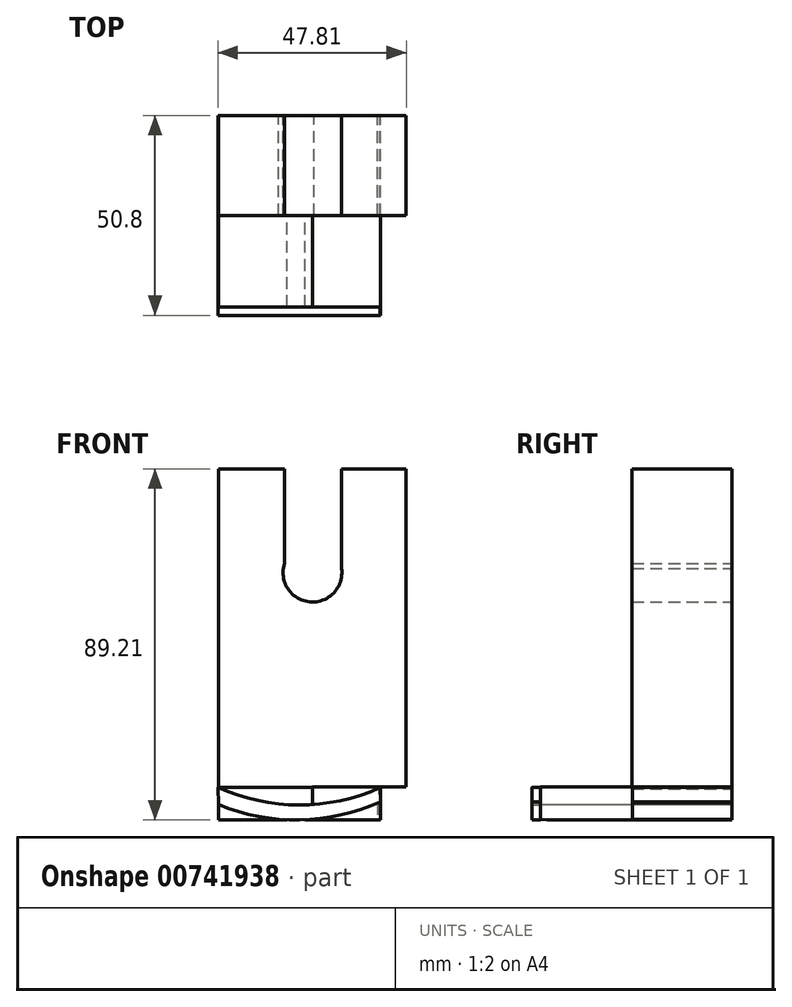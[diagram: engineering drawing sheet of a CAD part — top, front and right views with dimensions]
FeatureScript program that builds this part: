
annotation { "Feature Type Name" : "Feature", "Feature Type Description" : "" }
export const myFeature = defineFeature(function(context is Context, id is Id, definition is map)
    precondition{}
    {
        {
            var Q0;
            Q0=qCreatedBy(makeId("Front.planeOp"),FACE);
            var sketch = newSketch(context, id + "F0", { "sketchPlane" : qUnion([Q0])});
            skLineSegment(sketch, "E0.bottom", {"start": v(23.82, 44.5) * mm, "end": v(-23.82, 44.5) * mm});
            skLineSegment(sketch, "E0.top", {"start": v(16.53, -44.5) * mm, "end": v(-23.82, -44.5) * mm});
            skLineSegment(sketch, "E0.left", {"start": v(23.82, 44.5) * mm, "end": v(23.82, -36.31) * mm});
            skLineSegment(sketch, "E0.right", {"start": v(-23.82, 44.5) * mm, "end": v(-23.82, -44.5) * mm});
            skPoint(sketch, "E0.middle", {"position": v(0, 0) * mm});
            skLineSegment(sketch, "E1.bottom", {"start": v(-7.1, 44.5) * mm, "end": v(7.4, 44.5) * mm});
            skLineSegment(sketch, "E1.top", {"start": v(0, 18.15) * mm, "end": v(0.15, 18.15) * mm});
            skLineSegment(sketch, "E1.left", {"start": v(-7.1, 44.5) * mm, "end": v(-7.1, 18.15) * mm});
            skLineSegment(sketch, "E1.right", {"start": v(7.4, 44.5) * mm, "end": v(7.4, 18.15) * mm});
            skArc(sketch, "E2", {"start": v(-7.1, 20.49) * mm, "mid": v(-0.68, 10.7) * mm, "end": v(7.4, 19.17) * mm});
            skPoint(sketch, "E2.centerSnap0", {"position": v(0.15, 18.15) * mm});
            skLineSegment(sketch, "E3", {"start": v(23.82, -36.31) * mm, "end": v(16.53, -36.31) * mm});
            skLineSegment(sketch, "E4", {"start": v(16.53, -36.31) * mm, "end": v(16.53, -44.5) * mm});
            skPoint(sketch, "E5.orphan", {"position": v(23.82, -44.5) * mm});
            skSolve(sketch);
        }
        {
            var Q0;
            Q0=makeQuery(id+"F0.imprint","IMPRINT",FACE,{"disambiguationData":[TD([[makeQuery(id+"F0.imprint","IMPRINT",EDGE,{"derivedFrom":sQuery(id+"F0.wireOp",EDGE,"E0.top")}),-1.0]])]});
            extrude(context, id + "F1", {"entities" : qUnion([Q0]), "depth" : 25.4 * mm, "offsetDistance" : 25.4 * mm});
        }
        {
            var Q0;
            Q0=qCreatedBy(makeId("Right.planeOp"),FACE);
            var sketch = newSketch(context, id + "F2", { "sketchPlane" : qUnion([Q0])});
            skLineSegment(sketch, "E6", {"start": v(-25.4, -36.35) * mm, "end": v(-48.64, -36.35) * mm});
            skLineSegment(sketch, "E7", {"start": v(-48.64, -36.35) * mm, "end": v(-48.64, -44.71) * mm});
            skLineSegment(sketch, "E8", {"start": v(-48.64, -44.71) * mm, "end": v(-25.33, -44.58) * mm});
            skLineSegment(sketch, "E9", {"start": v(-25.33, -44.58) * mm, "end": v(-25.4, -36.35) * mm});
            skSolve(sketch);
        }
        {
            var Q0;
            Q0=makeQuery(id+"F2.imprint","IMPRINT",FACE,{"disambiguationData":[TD([[makeQuery(id+"F2.imprint","IMPRINT",EDGE,{"derivedFrom":sQuery(id+"F2.wireOp",EDGE,"E6")}),1.0]])]});
            extrude(context, id + "F3", {"entities" : qUnion([Q0]), "operationType" : NewBodyOperationType.ADD, "depth" : 17.27 * mm, "offsetDistance" : 25.4 * mm});
        }
        {
            var Q0;
            Q0=qCreatedBy(makeId("Right.planeOp"),FACE);
            var sketch = newSketch(context, id + "F4", { "sketchPlane" : qUnion([Q0])});
            skLineSegment(sketch, "E10.bottom", {"start": v(-25.35, -36.37) * mm, "end": v(-48.66, -36.37) * mm});
            skLineSegment(sketch, "E10.top", {"start": v(-25.35, -44.65) * mm, "end": v(-48.66, -44.65) * mm});
            skLineSegment(sketch, "E10.left", {"start": v(-25.35, -36.37) * mm, "end": v(-25.35, -44.65) * mm});
            skLineSegment(sketch, "E10.right", {"start": v(-48.66, -36.37) * mm, "end": v(-48.66, -44.65) * mm});
            skSolve(sketch);
        }
        {
            var Q0;
            Q0 = qSketchRegion(id + "F4", true);
            extrude(context, id + "F5", {"entities" : qUnion([Q0]), "operationType" : NewBodyOperationType.ADD, "oppositeDirection" : true, "depth" : 23.88 * mm, "offsetDistance" : 25.4 * mm});
        }
        {
            var Q0;
            Q0=qCreatedBy(makeId("Front.planeOp"),FACE);
            var sketch = newSketch(context, id + "F6", { "sketchPlane" : qUnion([Q0])});
            skArc(sketch, "E11", {"start": v(-24, -36.4) * mm, "mid": v(-3.42, -40.9) * mm, "end": v(17.17, -36.48) * mm});
            skArc(sketch, "E12", {"start": v(-23.92, -40.75) * mm, "mid": v(-3.27, -44.7) * mm, "end": v(17.24, -40.05) * mm});
            skLineSegment(sketch, "E13", {"start": v(-24, -36.4) * mm, "end": v(-23.92, -40.75) * mm});
            skLineSegment(sketch, "E14", {"start": v(17.17, -36.48) * mm, "end": v(17.24, -40.05) * mm});
            skLineSegment(sketch, "E15", {"start": v(17.13, -40.1) * mm, "end": v(17.17, -36.48) * mm});
            skLineSegment(sketch, "E16", {"start": v(16.98, -36.6) * mm, "end": v(16.88, -36.6) * mm});
            skPoint(sketch, "E17.end.orphan", {"position": v(-23.92, -44.73) * mm});
            skSolve(sketch);
        }
        {
            var Q0;
            Q0 = qSketchRegion(id + "F6", true);
            extrude(context, id + "F7", {"entities" : qUnion([Q0]), "operationType" : NewBodyOperationType.ADD, "depth" : 50.8 * mm, "offsetDistance" : 25.4 * mm});
        }
    });
